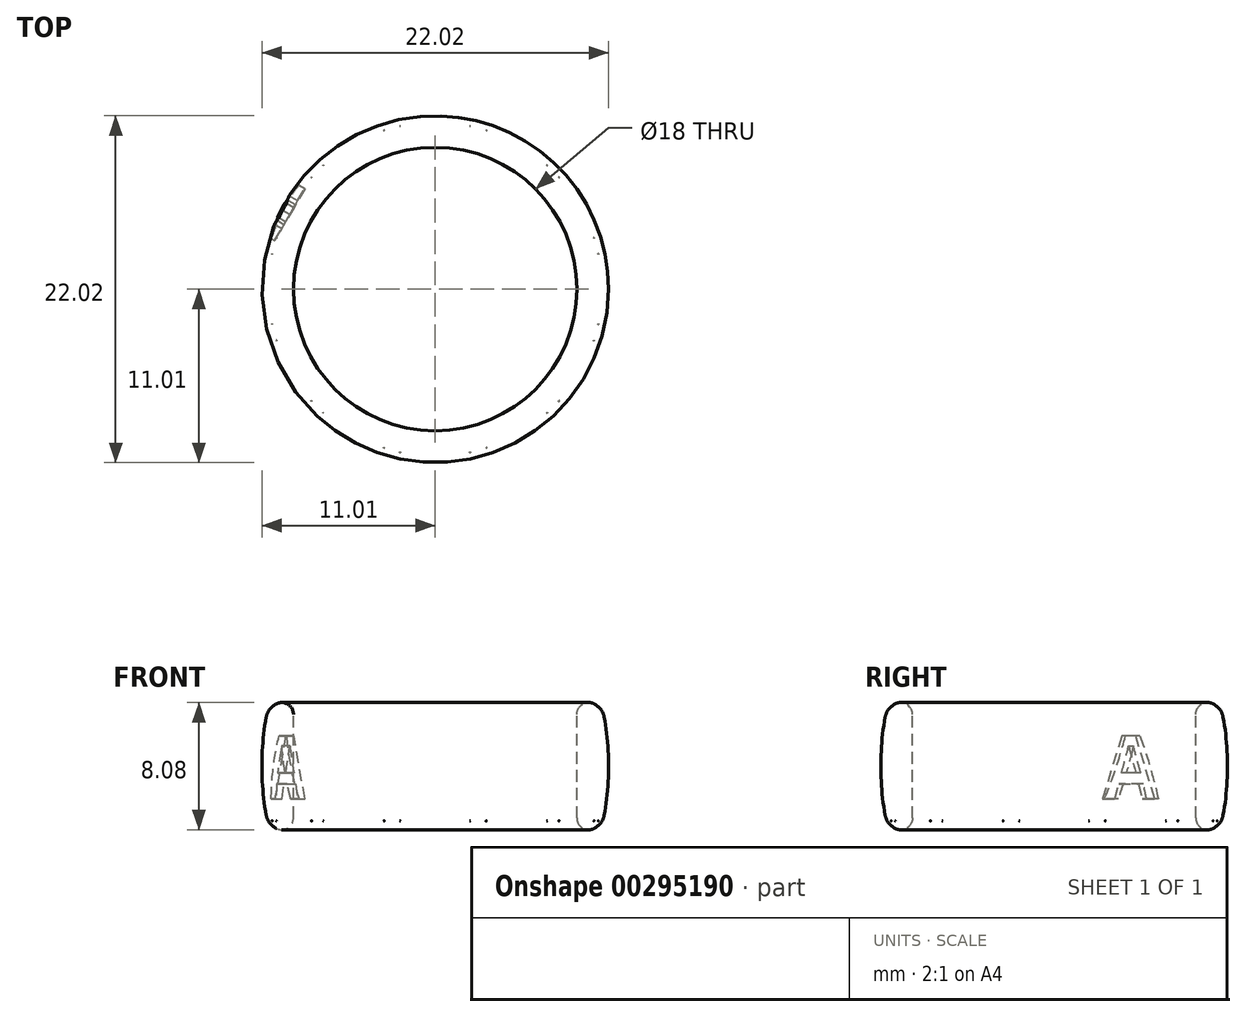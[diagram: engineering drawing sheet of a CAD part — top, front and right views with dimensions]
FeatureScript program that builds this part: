
annotation { "Feature Type Name" : "Feature", "Feature Type Description" : "" }
export const myFeature = defineFeature(function(context is Context, id is Id, definition is map)
    precondition{}
    {
        {
            var Q0;
            Q0=qCreatedBy(makeId("Top.planeOp"),FACE);
            var sketch = newSketch(context, id + "F0", { "sketchPlane" : qUnion([Q0])});
            skCircle(sketch, "E0", {"center": v(0, 0) * mm, "radius": 7.5 * mm});
            skSolve(sketch);
        }
        {
            var Q0;
            Q0=qSketchRegion(id+"F0",true);
            extrude(context, id + "F1", {"entities" : qUnion([Q0]), "depth" : 5 * mm});
        }
        {
            var Q0;
            Q0=qCreatedBy(makeId("Front.planeOp"),FACE);
            var sketch = newSketch(context, id + "F2", { "sketchPlane" : qUnion([Q0])});
            skLineSegment(sketch, "E1", {"start": v(-9, 0) * mm, "end": v(-9, 8.18) * mm});
            skLineSegment(sketch, "E2", {"start": v(-9, 8.18) * mm, "end": v(-10.5, 8.18) * mm});
            skLineSegment(sketch, "E3", {"start": v(-9, 0) * mm, "end": v(-10.5, 0) * mm});
            skEllipticalArc(sketch, "E4", {});
            const initialGuessF2  = {"E4": [-0.009, 0.004088467297574947, 0, 1, 0.006151676925641073, 0.0020075208455440164, 0.8438243033653899, 2.2977683502244024]};
            skSetInitialGuess(sketch, initialGuessF2);
            skSolve(sketch);
        }
        {
            var Q0;
            Q0=makeQuery(id+"F2.imprint","IMPRINT",FACE,{"disambiguationData":[TD([[makeQuery(id+"F2.imprint","IMPRINT",EDGE,{"derivedFrom":sQuery(id+"F2.wireOp",EDGE,"E1")}),1.0]])]});
            var Q1;
            Q1=makeQuery(id+"F1.opExtrude","SWEPT_FACE",FACE,{"disambiguationData":[OSD([sQuery(id+"F0.wireOp",EDGE,"E0")])]});
            revolve(context, id + "F3", {"entities" : qUnion([Q0]), "axis" : qUnion([Q1]), "revolveType" : RevolveType.FULL});
        }
        {
            var Q0;
            Q0=makeQuery(id+"F3.opRevolve","SWEPT_EDGE",EDGE,{"disambiguationData":[OSD([sQuery(id+"F2.wireOp",EDGE,"E2"),sQuery(id+"F2.wireOp",EDGE,"E4")])]});
            var Q1;
            Q1=makeQuery(id+"F3.opRevolve","SWEPT_EDGE",EDGE,{"disambiguationData":[OSD([sQuery(id+"F2.wireOp",EDGE,"E3"),sQuery(id+"F2.wireOp",EDGE,"E4")])]});
            fillet(context, id + "F4", {"entities" : qUnion([Q0, Q1]), "radius" : 1.2 * mm, "tangentPropagation" : true, "allowEdgeOverflow" : false});
        }
        {
            var Q0;
            Q0=makeQuery(id+"F3.opRevolve","SWEPT_EDGE",EDGE,{"disambiguationData":[OSD([sQuery(id+"F2.wireOp",EDGE,"E1"),sQuery(id+"F2.wireOp",EDGE,"E3")])]});
            var Q1;
            Q1=makeQuery(id+"F3.opRevolve","SWEPT_EDGE",EDGE,{"disambiguationData":[OSD([sQuery(id+"F2.wireOp",EDGE,"E1"),sQuery(id+"F2.wireOp",EDGE,"E2")])]});
            fillet(context, id + "F5", {"entities" : qUnion([Q0, Q1]), "radius" : .75 * mm, "tangentPropagation" : true, "allowEdgeOverflow" : false});
        }
        {
            var Q0;
            Q0=makeQuery(id+"F1.opExtrude","SWEPT_BODY",BODY,{"disambiguationData":[OSD([sQuery(id+"F0.wireOp",EDGE,"E0")])]});
            deleteBodies(context, id + "F6", {"entities" : qUnion([Q0])});
        }
        {
            var Q0;
            Q0=qCreatedBy(makeId("Top.planeOp"),FACE);
            cPlane(context, id + "F7", {"entities" : qUnion([Q0]), "cplaneType" : CPlaneType.OFFSET, "offset" : 7 * mm, "width" : 150 * mm, "height" : 150 * mm});
        }
        {
            var Q0;
            Q0=qCreatedBy(id+"F7.planeOp",FACE);
            var sketch = newSketch(context, id + "F8", { "sketchPlane" : qUnion([Q0])});
            skLineSegment(sketch, "E5.bottom", {"start": v(-2.25, -9.36) * mm, "end": v(2.25, -9.36) * mm});
            skLineSegment(sketch, "E5.top", {"start": v(-2.25, -10.36) * mm, "end": v(2.25, -10.36) * mm});
            skLineSegment(sketch, "E5.left", {"start": v(-2.25, -9.36) * mm, "end": v(-2.25, -10.36) * mm});
            skLineSegment(sketch, "E5.right", {"start": v(2.25, -9.36) * mm, "end": v(2.25, -10.36) * mm});
            skLineSegment(sketch, "E6.1.0", {"start": v(2.73, -9.23) * mm, "end": v(6.63, -6.98) * mm});
            skLineSegment(sketch, "E6.1.1", {"start": v(6.63, -6.98) * mm, "end": v(7.13, -7.85) * mm});
            skLineSegment(sketch, "E6.1.2", {"start": v(3.23, -10.1) * mm, "end": v(7.13, -7.85) * mm});
            skLineSegment(sketch, "E6.1.3", {"start": v(2.73, -9.23) * mm, "end": v(3.23, -10.1) * mm});
            skLineSegment(sketch, "E6.2.0", {"start": v(6.98, -6.63) * mm, "end": v(9.23, -2.73) * mm});
            skLineSegment(sketch, "E6.2.1", {"start": v(9.23, -2.73) * mm, "end": v(10.1, -3.23) * mm});
            skLineSegment(sketch, "E6.2.2", {"start": v(7.85, -7.13) * mm, "end": v(10.1, -3.23) * mm});
            skLineSegment(sketch, "E6.2.3", {"start": v(6.98, -6.63) * mm, "end": v(7.85, -7.13) * mm});
            skLineSegment(sketch, "E6.3.0", {"start": v(9.36, -2.25) * mm, "end": v(9.36, 2.25) * mm});
            skLineSegment(sketch, "E6.3.1", {"start": v(9.36, 2.25) * mm, "end": v(10.36, 2.25) * mm});
            skLineSegment(sketch, "E6.3.2", {"start": v(10.36, -2.25) * mm, "end": v(10.36, 2.25) * mm});
            skLineSegment(sketch, "E6.3.3", {"start": v(9.36, -2.25) * mm, "end": v(10.36, -2.25) * mm});
            skLineSegment(sketch, "E6.4.0", {"start": v(9.23, 2.73) * mm, "end": v(6.98, 6.63) * mm});
            skLineSegment(sketch, "E6.4.1", {"start": v(6.98, 6.63) * mm, "end": v(7.85, 7.13) * mm});
            skLineSegment(sketch, "E6.4.2", {"start": v(10.1, 3.23) * mm, "end": v(7.85, 7.13) * mm});
            skLineSegment(sketch, "E6.4.3", {"start": v(9.23, 2.73) * mm, "end": v(10.1, 3.23) * mm});
            skLineSegment(sketch, "E6.5.0", {"start": v(6.63, 6.98) * mm, "end": v(2.73, 9.23) * mm});
            skLineSegment(sketch, "E6.5.1", {"start": v(2.73, 9.23) * mm, "end": v(3.23, 10.1) * mm});
            skLineSegment(sketch, "E6.5.2", {"start": v(7.13, 7.85) * mm, "end": v(3.23, 10.1) * mm});
            skLineSegment(sketch, "E6.5.3", {"start": v(6.63, 6.98) * mm, "end": v(7.13, 7.85) * mm});
            skLineSegment(sketch, "E6.6.0", {"start": v(2.25, 9.36) * mm, "end": v(-2.25, 9.36) * mm});
            skLineSegment(sketch, "E6.6.1", {"start": v(-2.25, 9.36) * mm, "end": v(-2.25, 10.36) * mm});
            skLineSegment(sketch, "E6.6.2", {"start": v(2.25, 10.36) * mm, "end": v(-2.25, 10.36) * mm});
            skLineSegment(sketch, "E6.6.3", {"start": v(2.25, 9.36) * mm, "end": v(2.25, 10.36) * mm});
            skLineSegment(sketch, "E6.7.0", {"start": v(-2.73, 9.23) * mm, "end": v(-6.63, 6.98) * mm});
            skLineSegment(sketch, "E6.7.1", {"start": v(-6.63, 6.98) * mm, "end": v(-7.13, 7.85) * mm});
            skLineSegment(sketch, "E6.7.2", {"start": v(-3.23, 10.1) * mm, "end": v(-7.13, 7.85) * mm});
            skLineSegment(sketch, "E6.7.3", {"start": v(-2.73, 9.23) * mm, "end": v(-3.23, 10.1) * mm});
            skLineSegment(sketch, "E6.8.0", {"start": v(-6.98, 6.63) * mm, "end": v(-9.23, 2.73) * mm});
            skLineSegment(sketch, "E6.8.1", {"start": v(-9.23, 2.73) * mm, "end": v(-10.1, 3.23) * mm});
            skLineSegment(sketch, "E6.8.2", {"start": v(-7.85, 7.13) * mm, "end": v(-10.1, 3.23) * mm});
            skLineSegment(sketch, "E6.8.3", {"start": v(-6.98, 6.63) * mm, "end": v(-7.85, 7.13) * mm});
            skLineSegment(sketch, "E6.9.0", {"start": v(-9.36, 2.25) * mm, "end": v(-9.36, -2.25) * mm});
            skLineSegment(sketch, "E6.9.1", {"start": v(-9.36, -2.25) * mm, "end": v(-10.36, -2.25) * mm});
            skLineSegment(sketch, "E6.9.2", {"start": v(-10.36, 2.25) * mm, "end": v(-10.36, -2.25) * mm});
            skLineSegment(sketch, "E6.9.3", {"start": v(-9.36, 2.25) * mm, "end": v(-10.36, 2.25) * mm});
            skLineSegment(sketch, "E6.10.0", {"start": v(-9.23, -2.73) * mm, "end": v(-6.98, -6.63) * mm});
            skLineSegment(sketch, "E6.10.1", {"start": v(-6.98, -6.63) * mm, "end": v(-7.85, -7.13) * mm});
            skLineSegment(sketch, "E6.10.2", {"start": v(-10.1, -3.23) * mm, "end": v(-7.85, -7.13) * mm});
            skLineSegment(sketch, "E6.10.3", {"start": v(-9.23, -2.73) * mm, "end": v(-10.1, -3.23) * mm});
            skLineSegment(sketch, "E6.11.0", {"start": v(-6.63, -6.98) * mm, "end": v(-2.73, -9.23) * mm});
            skLineSegment(sketch, "E6.11.1", {"start": v(-2.73, -9.23) * mm, "end": v(-3.23, -10.1) * mm});
            skLineSegment(sketch, "E6.11.2", {"start": v(-7.13, -7.85) * mm, "end": v(-3.23, -10.1) * mm});
            skLineSegment(sketch, "E6.11.3", {"start": v(-6.63, -6.98) * mm, "end": v(-7.13, -7.85) * mm});
            skPoint(sketch, "E6.center", {"position": v(0, 0) * mm});
            skSolve(sketch);
        }
        {
            var Q0;
            Q0=qSketchRegion(id+"F8",true);
            extrude(context, id + "F9", {"entities" : qUnion([Q0]), "operationType" : NewBodyOperationType.ADD, "oppositeDirection" : true, "depth" : 6.4 * mm});
        }
        {
            var Q0;
            Q0=makeQuery(id+"F9.opExtrude","SWEPT_FACE",FACE,{"disambiguationData":[OSD([sQuery(id+"F8.wireOp",EDGE,"E6.8.2")])]});
            var sketch = newSketch(context, id + "F10", { "sketchPlane" : qUnion([Q0])});
            skText(sketch, "E7", { "text": "A", "fontName": "OpenSans-Bold.ttf"});
            const initialGuessF10  = {"E7": [-0.0014, 0.00202, 1, 0, 0.004]};
            skSetInitialGuess(sketch, initialGuessF10);
            skSolve(sketch);
        }
        {
            var Q0;
            Q0=qSketchRegion(id+"F10",true);
            extrude(context, id + "F11", {"entities" : qUnion([Q0]), "operationType" : NewBodyOperationType.REMOVE, "depth" : 1 * mm});
        }
    });
